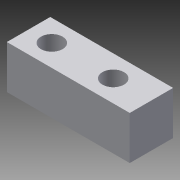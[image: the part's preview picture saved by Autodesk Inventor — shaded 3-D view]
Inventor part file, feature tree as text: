
AUTODESK INVENTOR PART (.ipt)
format: ipt  version: 2013 (Build 170138000, 138)  size: 84,992 bytes
history: native  units: mm
features: extrude x1, sketch x1
ambient origin geometry x8: Origin, YZ Plane, XZ Plane, XY Plane, X Axis, Y Axis, Z Axis, Center Point
bodies: Solid1 (feature_tree)
feature tree (2):
  extrude  "Extrusion1"  [1 undecoded]
  sketch  "Sketch1"  dims[d0=6.0mm d1=0.0mm]
note: 1 required parameter value undecoded (feature->parameter linkage not recoverable at this tier; creation-order binding heuristic only, values carry confidence <= 0.55)
